# Revit family: Hager-VOLTA-Flush_mounted-IP30-With_Cover-Without_DIN-Hosted-DE-de
name_source: partatom
category: Electrical Equipment
units: mm (PartAtom-declared; Revit-internal decimal feet)

## family parameters
Cut with Voids When Loaded = No
Host = Face
Maintain Annotation Orientation = Yes
Panel Configuration = Two Columns, Circuits Across
Part Type = Panelboard
Room Calculation Point = No
Round Connector Dimension = Use Diameter
Shared = No

## types (6) — shared parameters
BC_MODEL_ID = 1547153
BC_OBJECT_ID = 513475
BC_OBJECT_VERSION = #3
Code hager = ADD-EC000214_EU
EF000003 - Montageart = Unterputz
EF000007 - Farbe = weiß
EF000008 - Breite = 348 mm  [stored 1.14173 ft]
EF000024 - UV-beständig = No
EF000116 - RAL-Nummer = 9010
EF001062 - EMV-Ausführung = No
EF001088 - Anbaumöglichkeit = Yes
EF001134 - DIN-Schiene = No
EF002950 - Breite in Teilungseinheiten = 12
EF004462 - Art der Schließung = sonstige
EF005474 - Schutzart (IP) = IP30
EF006244 - Transparenter Deckel/Tür = No
EF006306 - Mit Schloss = No
EF009212 - Ausführung Deckel = mit Ausschnitt
ETIM class code = EC000214
ETIM class name = Small distribution board
HG000002-Mit tür = Yes
HG000003-Bereich = VOLTA
HG000005-Dicke = 2 mm  [stored 0.00656168 ft]
HG000006-Flush mounted = Yes
HG000009-Doppelflügeligen Tür = No
HG000010-Asymmetrische Türen = No
HG000011-Leere Reihen von unten = No
HG000012-Türschwenkwinkel = 90.00°
HG000013-Tür links = No
HG000014-Tür rechts = Yes
HG000015-Sichtbarkeit der Türöffnung = Yes
HG000016-3D-Türsichtbarkeit = Yes
HG000017-Distanz zwischen den Polen = 18 mm  [stored 0.0590551 ft]
HG000060-RAL-number = 9010
HG000099-Onfly Template ID-de-DE = 507532
HGEF0002950-Breite in Teilungseinheiten = 12
Manufacturer = Hager
Name = VOLTA-Flush_mounted-IP30-With_Cover-Without_DIN-DE
Name BIM&CO = Electricity
Name hager = ADD_Enclosures_EC000214
Uniformat = Low Tension Service & Dist.
Uniformat code = D501001
zero-valued in all types: Default Elevation, EF000266 - Anzahl der Reihen, EF001131 - Innentiefe, HG000007-Anzahl der leeren Spalten, HG000008-Anzahl der leeren Reihen, HGEF000266-Anzahl der Reihen

## per-type parameters (varying)
| type | BC_VARIANT_ID | EF000040 - Höhe | EF000049 - Tiefe | EF000118 - Mit Montageplatte | EF000218 - Einbautiefe | EF000332 - Einbauhöhe | EF000846 - Einbaubreite | EF015776 - Erdungsklemmenblock | EF015777 - Neutralleiterklemmenblock | EF015941 - Signaldurchlassende Tür | HG000001-Anzahl der Spalten | HG000004-Herstellerreferenz |
| VOLTA-Flush_mounted_W348_H505_D94_12_Modular_Spacing-VU24NCT | 1174219 | 505 mm  [stored 1.65682 ft] | 94 mm  [stored 0.308399 ft] | No | 90 mm  [stored 0.295276 ft] | 490 mm  [stored 1.60761 ft] | 335 mm  [stored 1.09908 ft] | No | No | No | 1 | VU24NCT |
| VOLTA-Flush_mounted_W348_H630_D98_12_Modular_Spacing-VU36NW | 1174220 | 630 mm  [stored 2.06693 ft] | 98 mm  [stored 0.321522 ft] | Yes | 89 mm  [stored 0.291995 ft] | 595 mm  [stored 1.9521 ft] | 315 mm | Yes | Yes | No | 0 | VU36NW |
| VOLTA-Flush_mounted_W348_H755_D98_12_Modular_Spacing-VU48NW | 1174221 | 755 mm  [stored 2.47703 ft] | 98 mm  [stored 0.321522 ft] | Yes | 89 mm  [stored 0.291995 ft] | 720 mm  [stored 2.3622 ft] | 315 mm | No | No | No | 0 | VU48NW |
| VOLTA-Flush_mounted_W348_H755_D98_12_Modular_Spacing-VU48WWH | 1174222 | 755 mm  [stored 2.47703 ft] | 98 mm  [stored 0.321522 ft] | Yes | 89 mm  [stored 0.291995 ft] | 720 mm  [stored 2.3622 ft] | 315 mm | Yes | Yes | Yes | 0 | VU48WWH |
| VOLTA-Flush_mounted_W348_H880_D98_12_Modular_Spacing-VU60NW | 1174223 | 880 mm  [stored 2.88714 ft] | 98 mm  [stored 0.321522 ft] | Yes | 89 mm  [stored 0.291995 ft] | 845 mm  [stored 2.77231 ft] | 315 mm | Yes | Yes | No | 0 | VU60NW |
| VOLTA-Flush_mounted_W348_H880_D98_12_Modular_Spacing-VU60WWH | 1174224 | 880 mm  [stored 2.88714 ft] | 98 mm  [stored 0.321522 ft] | Yes | 89 mm  [stored 0.291995 ft] | 845 mm  [stored 2.77231 ft] | 315 mm | Yes | Yes | Yes | 0 | VU60WWH |

note: column(s) folded — value = type name in every type: Reference

note: [stored X ft] marks values corroborated as IEEE doubles in the binary element streams (Revit-internal decimal feet)

## geometry (parser evidence)
native form markers: Sweep x14
no freeform markers — native parametric forms only
